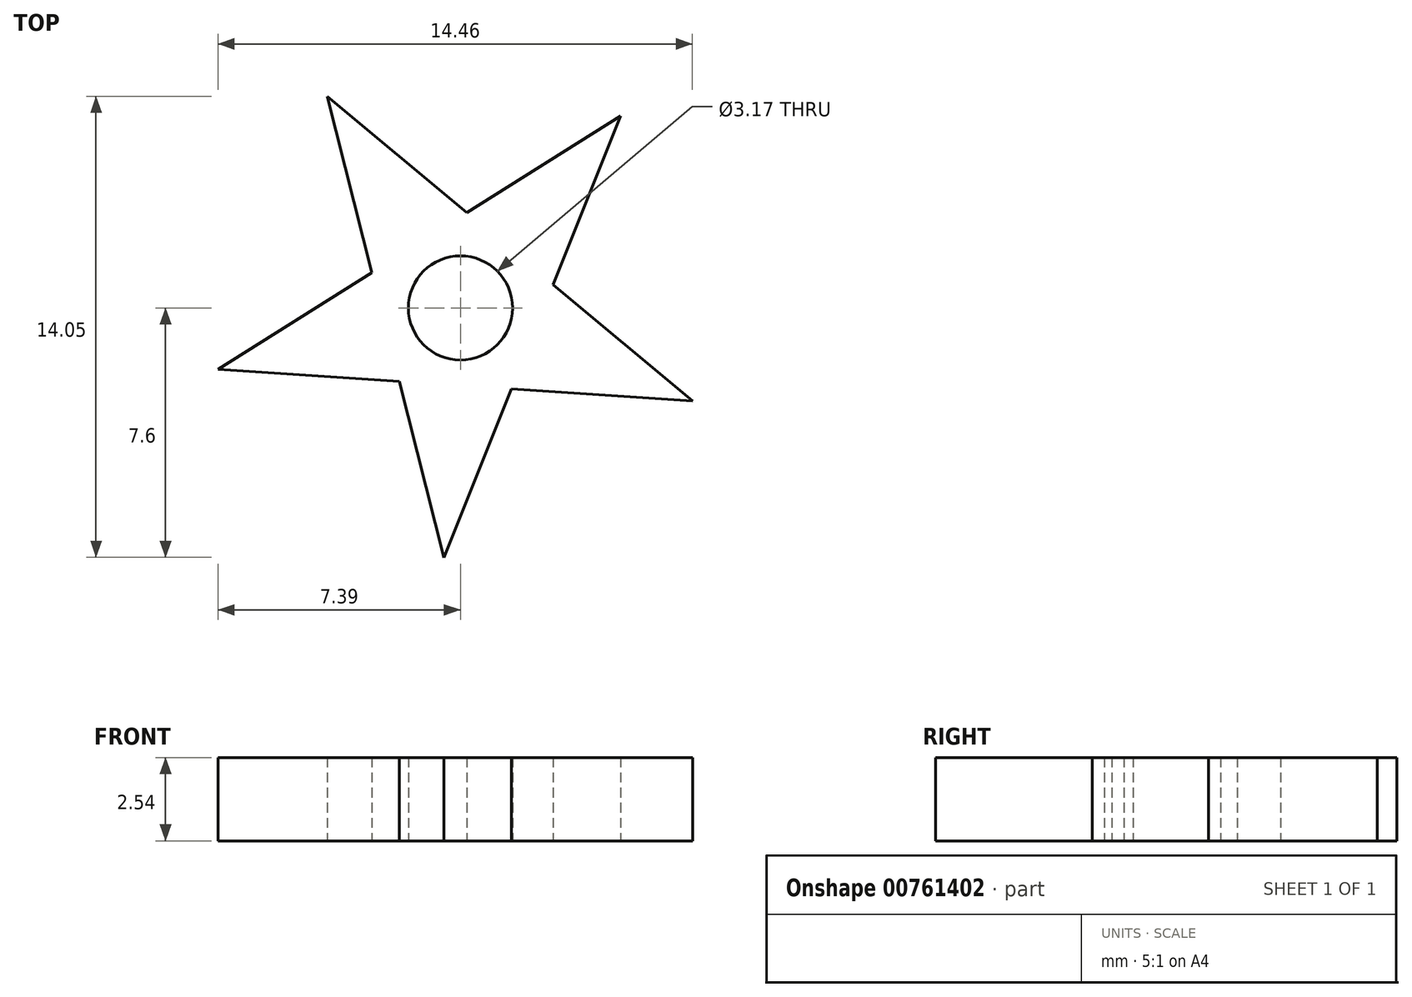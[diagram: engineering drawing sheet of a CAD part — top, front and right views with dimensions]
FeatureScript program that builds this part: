
annotation { "Feature Type Name" : "Feature", "Feature Type Description" : "" }
export const myFeature = defineFeature(function(context is Context, id is Id, definition is map)
    precondition{}
    {
        {
            var Q0;
            Q0=qCreatedBy(makeId("Top.planeOp"),FACE);
            var sketch = newSketch(context, id + "F0", { "sketchPlane" : qUnion([Q0])});
            skLineSegment(sketch, "E0", {"start": v(-4.06, 6.45) * mm, "end": v(-2.7, 1.08) * mm});
            skLineSegment(sketch, "E1", {"start": v(4.88, 5.85) * mm, "end": v(2.82, 0.71) * mm});
            skLineSegment(sketch, "E2", {"start": v(-7.39, -1.87) * mm, "end": v(-1.86, -2.24) * mm});
            skLineSegment(sketch, "E3", {"start": v(-7.39, -1.87) * mm, "end": v(-2.7, 1.08) * mm});
            skLineSegment(sketch, "E4", {"start": v(7.07, -2.83) * mm, "end": v(2.82, 0.71) * mm});
            skCircle(sketch, "E5", {"center": v(0, 0) * mm, "radius": 1.59 * mm});
            skLineSegment(sketch, "E6.trimOffspring", {"start": v(-1.86, -2.24) * mm, "end": v(-0.5, -7.6) * mm});
            skLineSegment(sketch, "E7.trimOffspring", {"start": v(0.2, 2.9) * mm, "end": v(4.88, 5.85) * mm});
            skLineSegment(sketch, "E8.trimOffspring", {"start": v(0.2, 2.9) * mm, "end": v(-4.06, 6.45) * mm});
            skLineSegment(sketch, "E9.trimOffspring", {"start": v(1.55, -2.46) * mm, "end": v(-0.5, -7.6) * mm});
            skLineSegment(sketch, "E10.trimOffspring", {"start": v(1.55, -2.46) * mm, "end": v(7.07, -2.83) * mm});
            skSolve(sketch);
        }
        {
            var Q0;
            Q0=makeQuery(id+"F0.imprint","IMPRINT",FACE,{"disambiguationData":[TD([[makeQuery(id+"F0.imprint","IMPRINT",EDGE,{"derivedFrom":sQuery(id+"F0.wireOp",EDGE,"E0")}),1.0]])]});
            extrude(context, id + "F1", {"entities" : qUnion([Q0]), "depth" : 2.54 * mm, "offsetDistance" : 25.4 * mm});
        }
    });
